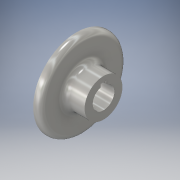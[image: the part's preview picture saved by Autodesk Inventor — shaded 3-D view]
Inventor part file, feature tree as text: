
AUTODESK INVENTOR PART (.ipt)
format: ipt  version: 2016 (Build 200138000, 138)  size: 167,424 bytes
history: native  units: in
note: dims shown in document units (in); Inventor stores cm internally (conversion verified against a paired STEP export)
features: sketch x2, revolve x1, extrude x1
ambient origin geometry x8: Origin, YZ Plane, XZ Plane, XY Plane, X Axis, Y Axis, Z Axis, Center Point
bodies: Solid1 (feature_tree)
feature tree (4):
  revolve  "Revolution1"  [1 undecoded]
  extrude  "Extrusion1"  Depth=0.625in
  sketch  "Sketch1"  dims[d0=2.0in d1=0.875in]
  sketch  "Sketch2"  dims[d2=0.0in d3=0.625in d4=0.1562in d5=0.125in d6=0.0312in d7=1.75in d8=0.5in d9=90.0deg d10=0.125in d11=0.0625in d12=0.0625in d13=0.125in d14=1.0in d15=0.0in]
note: 1 required parameter value undecoded (feature->parameter linkage not recoverable at this tier; creation-order binding heuristic only, values carry confidence <= 0.55)
